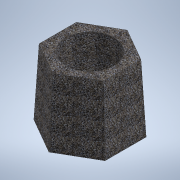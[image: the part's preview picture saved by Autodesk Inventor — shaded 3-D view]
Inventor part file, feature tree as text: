
AUTODESK INVENTOR PART (.ipt)
format: ipt  version: 2021 (Build 250183000, 183)  size: 146,944 bytes
history: native  units: mm
features: sketch x3, plane x1, loft x1, extrude x1
ambient origin geometry x8: Origin, YZ Plane, XZ Plane, XY Plane, X Axis, Y Axis, Z Axis, Center Point
bodies: Solid1 (feature_tree)
feature tree (6):
  sketch  "Sketch1"  dims[d0=750.0mm d1=700.0mm]
  plane  "Work Plane1"
  loft  "Loft1"
  extrude  "Extrusion1"  TaperAngle=0.0deg  [1 undecoded]
  sketch  "Sketch2"  dims[d2=680.0mm d3=0.0mm d4=90.0deg]
  sketch  "Sketch3"  dims[d5=0.0mm d6=90.0deg d7=510.0mm d8=620.0mm d9=0.0mm]
note: 1 required parameter value undecoded (feature->parameter linkage not recoverable at this tier; creation-order binding heuristic only, values carry confidence <= 0.55)
